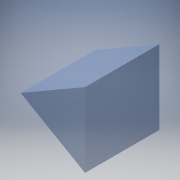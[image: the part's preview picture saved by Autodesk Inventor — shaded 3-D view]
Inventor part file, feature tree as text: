
AUTODESK INVENTOR PART (.ipt)
format: ipt  version: 2017 (Build 210142000, 142)  size: 92,672 bytes
history: native  units: mm
features: extrude x1, sketch x1
ambient origin geometry x8: Origin, YZ Plane, XZ Plane, XY Plane, X Axis, Y Axis, Z Axis, Center Point
bodies: Solid1 (feature_tree)
feature tree (2):
  extrude  "Extrusion1"  Depth=25.4mm TaperAngle=0.0deg
  sketch  "Sketch1"  dims[d0=25.4mm d1=25.4mm d2=0.0mm]
